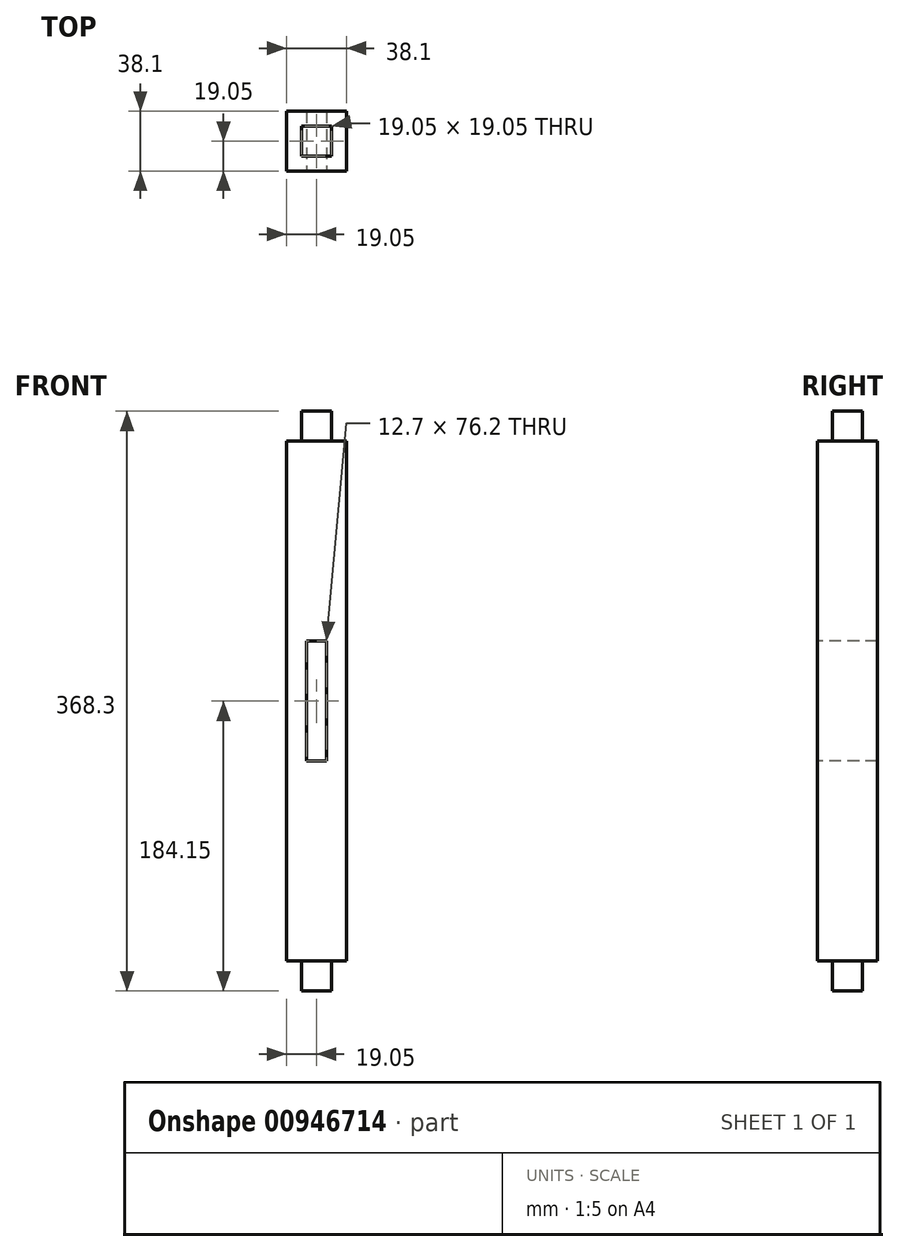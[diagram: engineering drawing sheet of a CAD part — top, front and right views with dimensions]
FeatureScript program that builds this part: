
annotation { "Feature Type Name" : "Feature", "Feature Type Description" : "" }
export const myFeature = defineFeature(function(context is Context, id is Id, definition is map)
    precondition{}
    {
        {
            var Q0;
            Q0=qCreatedBy(makeId("Top.planeOp"),FACE);
            var sketch = newSketch(context, id + "F0", { "sketchPlane" : qUnion([Q0])});
            skLineSegment(sketch, "E0.bottom", {"start": v(19.05, 19.05) * mm, "end": v(-19.05, 19.05) * mm});
            skLineSegment(sketch, "E0.top", {"start": v(19.05, -19.05) * mm, "end": v(-19.05, -19.05) * mm});
            skLineSegment(sketch, "E0.left", {"start": v(19.05, 19.05) * mm, "end": v(19.05, -19.05) * mm});
            skLineSegment(sketch, "E0.right", {"start": v(-19.05, 19.05) * mm, "end": v(-19.05, -19.05) * mm});
            skPoint(sketch, "E0.middle", {"position": v(0, 0) * mm});
            skSolve(sketch);
        }
        {
            var Q0;
            Q0 = qSketchRegion(id + "F0", true);
            extrude(context, id + "F1", {"entities" : qUnion([Q0]), "flatOperationType" : FlatOperationType.REMOVE, "depth" : 330.2 * mm, "offsetDistance" : 25.4 * mm, "domain" : OperationDomain.MODEL});
        }
        {
            var Q0;
            Q0=makeQuery(id+"F1.opExtrude","CAP_FACE",FACE,{"disambiguationData":[OSD([sQuery(id+"F0.wireOp",EDGE,"E0.bottom"),sQuery(id+"F0.wireOp",EDGE,"E0.top"),sQuery(id+"F0.wireOp",EDGE,"E0.left"),sQuery(id+"F0.wireOp",EDGE,"E0.right")])],"isStart":false});
            var sketch = newSketch(context, id + "F2", { "sketchPlane" : qUnion([Q0])});
            skLineSegment(sketch, "E1", {"start": v(-19.05, -19.05) * mm, "end": v(19.05, 19.05) * mm});
            skLineSegment(sketch, "E2.bottom", {"start": v(9.52, 9.53) * mm, "end": v(-9.52, 9.53) * mm});
            skLineSegment(sketch, "E2.top", {"start": v(9.52, -9.53) * mm, "end": v(-9.52, -9.53) * mm});
            skLineSegment(sketch, "E2.left", {"start": v(9.52, 9.53) * mm, "end": v(9.52, -9.53) * mm});
            skLineSegment(sketch, "E2.right", {"start": v(-9.52, 9.53) * mm, "end": v(-9.52, -9.53) * mm});
            skPoint(sketch, "E2.middle", {"position": v(0, 0) * mm});
            skSolve(sketch);
        }
        {
            var Q0;
            Q0 = qSketchRegion(id + "F2", true);
            extrude(context, id + "F3", {"entities" : qUnion([Q0]), "operationType" : NewBodyOperationType.ADD, "depth" : 19.05 * mm, "offsetDistance" : 25.4 * mm});
        }
        {
            var Q0;
            Q0=makeQuery(id+"F1.opExtrude","CAP_FACE",FACE,{"disambiguationData":[OSD([sQuery(id+"F0.wireOp",EDGE,"E0.bottom"),sQuery(id+"F0.wireOp",EDGE,"E0.top"),sQuery(id+"F0.wireOp",EDGE,"E0.left"),sQuery(id+"F0.wireOp",EDGE,"E0.right")])],"isStart":true});
            var sketch = newSketch(context, id + "F4", { "sketchPlane" : qUnion([Q0])});
            skLineSegment(sketch, "E3.bottom", {"start": v(9.53, -9.52) * mm, "end": v(-9.52, -9.53) * mm});
            skLineSegment(sketch, "E3.top", {"start": v(9.52, 9.53) * mm, "end": v(-9.53, 9.52) * mm});
            skLineSegment(sketch, "E3.left", {"start": v(9.53, -9.52) * mm, "end": v(9.52, 9.53) * mm});
            skLineSegment(sketch, "E3.right", {"start": v(-9.52, -9.53) * mm, "end": v(-9.53, 9.52) * mm});
            skPoint(sketch, "E3.middle", {"position": v(0, 0) * mm});
            skSolve(sketch);
        }
        {
            var Q0;
            Q0 = qSketchRegion(id + "F4", true);
            extrude(context, id + "F5", {"entities" : qUnion([Q0]), "operationType" : NewBodyOperationType.ADD, "depth" : 19.05 * mm, "offsetDistance" : 25.4 * mm});
        }
        {
            var Q0;
            Q0=makeQuery(id+"F1.opExtrude","SWEPT_FACE",FACE,{"disambiguationData":[OSD([sQuery(id+"F0.wireOp",EDGE,"E0.top")])]});
            var sketch = newSketch(context, id + "F6", { "sketchPlane" : qUnion([Q0])});
            skLineSegment(sketch, "E4", {"start": v(-19.05, 165.1) * mm, "end": v(19.05, 165.1) * mm});
            skLineSegment(sketch, "E5.bottom", {"start": v(6.35, 203.2) * mm, "end": v(-6.35, 203.2) * mm});
            skLineSegment(sketch, "E5.top", {"start": v(6.35, 127) * mm, "end": v(-6.35, 127) * mm});
            skLineSegment(sketch, "E5.left", {"start": v(6.35, 203.2) * mm, "end": v(6.35, 127) * mm});
            skLineSegment(sketch, "E5.right", {"start": v(-6.35, 203.2) * mm, "end": v(-6.35, 127) * mm});
            skPoint(sketch, "E5.middle", {"position": v(0, 165.1) * mm});
            skSolve(sketch);
        }
        {
            var Q0;
            Q0 = qSketchRegion(id + "F6", true);
            extrude(context, id + "F7", {"entities" : qUnion([Q0]), "operationType" : NewBodyOperationType.REMOVE, "endBound" : BoundingType.THROUGH_ALL, "oppositeDirection" : true, "depth" : 25.4 * mm, "offsetDistance" : 25.4 * mm});
        }
    });
